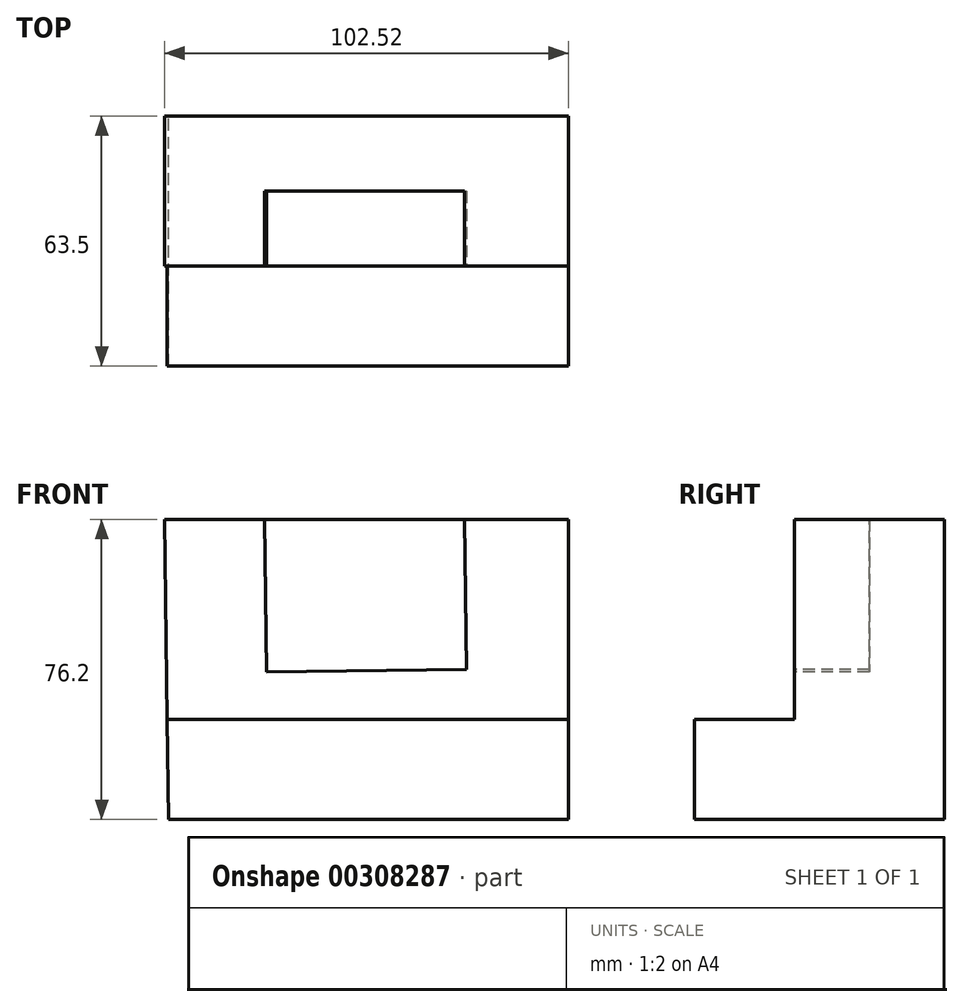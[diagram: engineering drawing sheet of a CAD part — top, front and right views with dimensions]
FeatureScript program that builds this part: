
annotation { "Feature Type Name" : "Feature", "Feature Type Description" : "" }
export const myFeature = defineFeature(function(context is Context, id is Id, definition is map)
    precondition{}
    {
        {
            var Q0;
            Q0=qCreatedBy(makeId("Front.planeOp"),FACE);
            var sketch = newSketch(context, id + "F0", { "sketchPlane" : qUnion([Q0])});
            skLineSegment(sketch, "E0", {"start": v(-50.34, -16.11) * mm, "end": v(51.26, -16.11) * mm});
            skLineSegment(sketch, "E1", {"start": v(51.26, -16.11) * mm, "end": v(51.26, 60.09) * mm});
            skLineSegment(sketch, "E2", {"start": v(51.26, 60.09) * mm, "end": v(-51.26, 60.09) * mm});
            skLineSegment(sketch, "E3", {"start": v(-51.26, 60.09) * mm, "end": v(-50.34, -16.11) * mm});
            skSolve(sketch);
        }
        {
            var Q0;
            Q0=makeQuery(id+"F0.imprint","IMPRINT",FACE,{"disambiguationData":[TD([[makeQuery(id+"F0.imprint","IMPRINT",EDGE,{"derivedFrom":sQuery(id+"F0.wireOp",EDGE,"E0")}),1.0]])]});
            extrude(context, id + "F1", {"entities" : qUnion([Q0]), "depth" : 63.5 * mm});
        }
        {
            var Q0;
            Q0=makeQuery(id+"F1.opExtrude","SWEPT_FACE",FACE,{"disambiguationData":[OSD([sQuery(id+"F0.wireOp",EDGE,"E1")])]});
            var sketch = newSketch(context, id + "F2", { "sketchPlane" : qUnion([Q0])});
            skLineSegment(sketch, "E4", {"start": v(-63.5, 9.29) * mm, "end": v(-38.1, 9.29) * mm});
            skLineSegment(sketch, "E5", {"start": v(-38.1, 9.29) * mm, "end": v(-38.1, 60.09) * mm});
            skSolve(sketch);
        }
        {
            var Q0;
            Q0 = qSketchRegion(id + "F2", true);
            var Q1;
            {var subQ0=sQuery(id+"F2.wireOp",EDGE,"E4");Q1=makeQuery(id+"F2.imprint","IMPRINT",FACE,{"disambiguationData":[TD([[makeQuery(id+"F2.imprint","IMPRINT",EDGE,{"derivedFrom":subQ0}),1.0]])]});}
            extrude(context, id + "F3", {"entities" : qUnion([Q0, Q1]), "operationType" : NewBodyOperationType.REMOVE, "oppositeDirection" : true, "depth" : 104.14 * mm});
        }
        {
            var Q0;
            Q0=makeQuery(id+"F3.boolean.opBoolean","COPY",FACE,{"derivedFrom":makeQuery(id+"F3.opExtrude","SWEPT_FACE",FACE,{"disambiguationData":[OSD([sQuery(id+"F2.wireOp",EDGE,"E5")])]})});
            var sketch = newSketch(context, id + "F4", { "sketchPlane" : qUnion([Q0])});
            skLineSegment(sketch, "E6", {"start": v(-25.86, 60.09) * mm, "end": v(-25.4, 21.37) * mm});
            skLineSegment(sketch, "E7", {"start": v(-25.4, 21.37) * mm, "end": v(25.4, 22) * mm});
            skLineSegment(sketch, "E8", {"start": v(25.4, 22) * mm, "end": v(24.94, 60.09) * mm});
            skLineSegment(sketch, "E9", {"start": v(-51.26, 60.09) * mm, "end": v(-25.86, 60.09) * mm});
            skSolve(sketch);
        }
        {
            var Q0;
            {var subQ0=sQuery(id+"F4.wireOp",EDGE,"E6");Q0=makeQuery(id+"F4.imprint","IMPRINT",FACE,{"disambiguationData":[TD([[makeQuery(id+"F4.imprint","IMPRINT",EDGE,{"derivedFrom":subQ0}),1.0]])]});}
            extrude(context, id + "F5", {"entities" : qUnion([Q0]), "operationType" : NewBodyOperationType.REMOVE, "oppositeDirection" : true, "depth" : 19.05 * mm});
        }
    });
